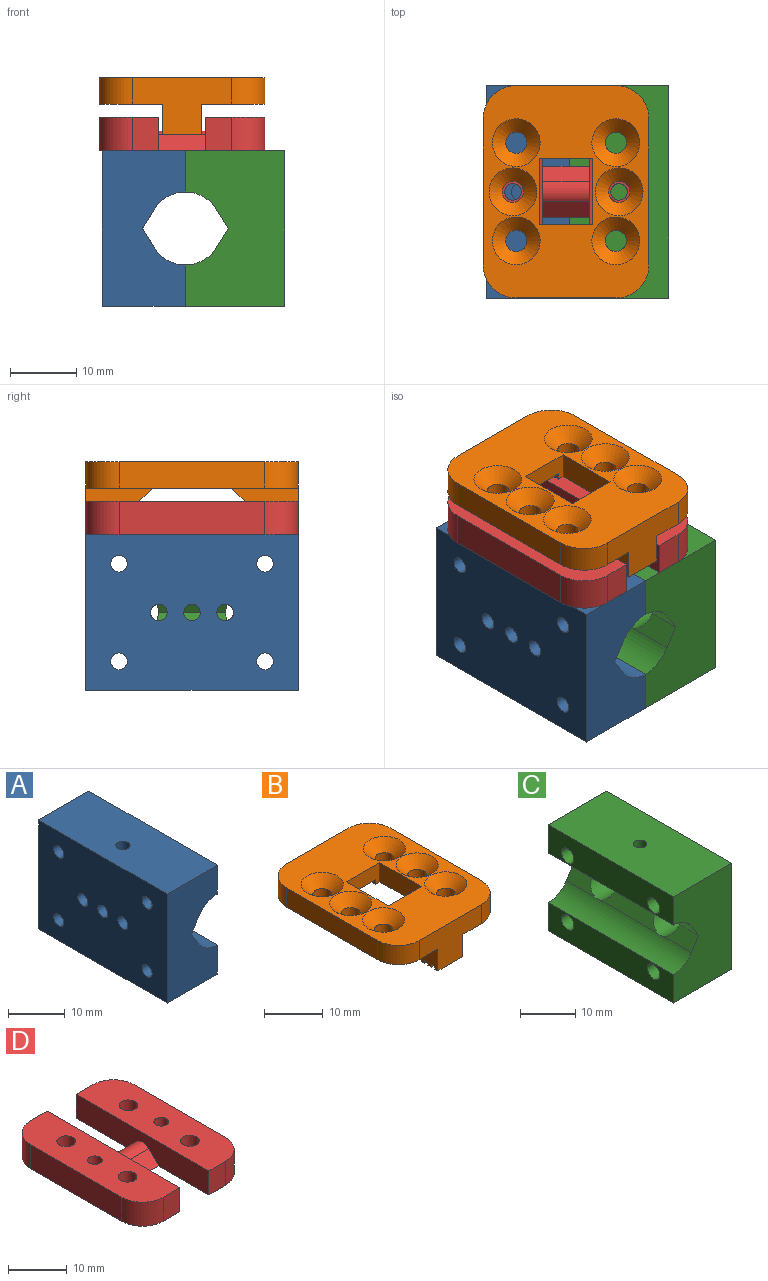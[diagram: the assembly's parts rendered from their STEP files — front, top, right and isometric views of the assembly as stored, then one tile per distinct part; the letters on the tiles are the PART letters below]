
ASSEMBLY  parts=4 mates=3
PART A: 20 faces, bbox 12.5x32x23.5 mm
  f0: plane 2.5x2.5mm, normal (0,0,1), area 4.9mm2, adj f6
  f1: cylinder r=1.25mm len=6.79mm, axis (1,0,0), area 51.1mm2, adj f4,f5,f13
  f2: cylinder r=1.25mm len=6.79mm, axis (1,0,0), area 51.1mm2, adj f4,f5,f13
  f3: cylinder r=1.25mm len=6.79mm, axis (1,0,0), area 51.1mm2, adj f4,f5,f13
  f4: plane 32x2.93mm, normal (0.85,0,0.53), area 102.1mm2, adj f1,f2,f3,f5,f16,f17,f18
  f5: plane 32x2.93mm, normal (0.85,0,-0.53), area 102.1mm2, adj f1,f2,f3,f4,f16,f17,f19
  f6: cylinder r=1.25mm len=10mm, axis (0,0,1), area 78.5mm2, adj f0,f14
  f7: cylinder r=1.25mm len=12.5mm, axis (1,0,0), area 98.2mm2, adj f12,f13
  f8: cylinder r=1.25mm len=12.5mm, axis (1,0,0), area 98.2mm2, adj f10,f13
  f9: cylinder r=1.25mm len=12.5mm, axis (1,0,0), area 98.2mm2, adj f10,f13
  f10: plane 32x6.25mm, normal (1,0,0), area 190.2mm2, adj f8,f9,f14,f16,f17,f19
  f11: cylinder r=1.25mm len=12.5mm, axis (1,0,0), area 98.2mm2, adj f12,f13
  f12: plane 32x6.25mm, normal (1,0,0), area 190.2mm2, adj f7,f11,f15,f16,f17,f18
  f13: plane 32x23.5mm, normal (-1,0,0), area 717.6mm2, adj f1,f2,f3,f7,f8,f9,f11,f14
  f14: plane 32x12.5mm, normal (0,0,1), area 395.1mm2, adj f6,f10,f13,f16,f17
  f15: plane 32x12.5mm, normal (0,0,-1), area 400mm2, adj f12,f13,f16,f17
  f16: plane 23.5x12.5mm, normal (0,1,0), area 244.2mm2, adj f4,f5,f10,f12,f13,f14,f15,f18
  f17: plane 23.5x12.5mm, normal (0,-1,0), area 244.2mm2, adj f4,f5,f10,f12,f13,f14,f15,f18
  f18: cylinder r=5.5mm len=32mm, axis (0,-1,0), area 177.5mm2, adj f4,f12,f16,f17
  f19: cylinder r=5.5mm len=32mm, axis (0,-1,0), area 177.5mm2, adj f5,f10,f16,f17
PART B: 59 faces, bbox 25x32x8.6 mm
  f0: plane 6x0.6mm, normal (0,1,0), area 3.6mm2, adj f1,f14,f15,f16
  f1: plane 6x0.8mm, normal (0,0,-1), area 4.8mm2, adj f0,f2,f15,f16
  f2: plane 6x0.6mm, normal (0,-1,0), area 3.6mm2, adj f1,f3,f15,f16
  f3: plane 6x0.8mm, normal (0,0,-1), area 4.8mm2, adj f2,f4,f15,f16
  f4: plane 6x0.6mm, normal (0,1,0), area 3.6mm2, adj f3,f5,f15,f16
  f5: plane 6x2mm, normal (0,0,-1), area 12mm2, adj f4,f6,f15,f16
  f6: plane 6x5mm, normal (0,0.71,-0.71), area 42.4mm2, adj f5,f7,f15,f16,f18,f24
  f7: plane 8x4mm, normal (0,1,0), area 26mm2, adj f6,f8,f18,f19,f20,f24,f25,f26
  f8: plane 32x25mm, normal (0,0,1), area 454.2mm2, adj f7,f9,f17,f20,f23,f26,f36,f37
  f9: plane 15x8.6mm, normal (0,-1,0), area 87.6mm2, adj f8,f10,f15,f16,f19,f25,f51,f52
  f10: plane 6x0.8mm, normal (0,0,-1), area 4.8mm2, adj f9,f11,f15,f16
  f11: plane 6x0.6mm, normal (0,1,0), area 3.6mm2, adj f10,f12,f15,f16
  f12: plane 6x0.8mm, normal (0,0,-1), area 4.8mm2, adj f11,f13,f15,f16
  f13: plane 6x0.6mm, normal (0,-1,0), area 3.6mm2, adj f12,f14,f15,f16
  f14: plane 6x0.8mm, normal (0,0,-1), area 4.8mm2, adj f0,f13,f15,f16
  f15: plane 10x4.6mm, normal (-1,0,0), area 33.4mm2, adj f0,f1,f2,f3,f4,f5,f6,f9
  f16: plane 10x4.6mm, normal (1,0,0), area 33.4mm2, adj f0,f1,f2,f3,f4,f5,f6,f9
  f17: plane 22x4mm, normal (-1,0,0), area 88mm2, adj f8,f19,f50,f52
  f18: plane 1x1mm, normal (1,0,0), area 0.5mm2, adj f6,f7,f19
  f19: plane 32x9.5mm, normal (0,0,-1), area 259.1mm2, adj f7,f9,f15,f17,f18,f20,f21,f22
  f20: plane 10x4mm, normal (1,0,0), area 40mm2, adj f7,f8,f19,f36
  f21: cylinder r=1.6mm len=3.2mm, axis (0,0,-1), area 20.1mm2, adj f19,f58
  f22: cylinder r=1.6mm len=3.2mm, axis (0,0,-1), area 20.1mm2, adj f19,f56
  f23: plane 22x4mm, normal (1,0,0), area 88mm2, adj f8,f25,f49,f51
  f24: plane 1x1mm, normal (-1,0,0), area 0.5mm2, adj f6,f7,f25
  f25: plane 32x9.5mm, normal (0,0,-1), area 259.1mm2, adj f7,f9,f16,f23,f24,f26,f27,f28
  f26: plane 10x4mm, normal (-1,0,0), area 40mm2, adj f7,f8,f25,f36
  f27: cylinder r=1.6mm len=3.2mm, axis (0,0,-1), area 20.1mm2, adj f25,f57
  f28: cylinder r=1.6mm len=3.2mm, axis (0,0,-1), area 20.1mm2, adj f25,f55
  f29: plane 6x0.6mm, normal (0,-1,0), area 3.6mm2, adj f30,f42,f43,f44
  f30: plane 6x0.8mm, normal (0,0,-1), area 4.8mm2, adj f29,f31,f43,f44
  f31: plane 6x0.6mm, normal (0,1,0), area 3.6mm2, adj f30,f32,f43,f44
  f32: plane 6x0.8mm, normal (0,0,-1), area 4.8mm2, adj f31,f33,f43,f44
  f33: plane 6x0.6mm, normal (0,-1,0), area 3.6mm2, adj f32,f34,f43,f44
  f34: plane 6x2mm, normal (0,0,-1), area 12mm2, adj f33,f35,f43,f44
  f35: plane 6x5mm, normal (0,-0.71,-0.71), area 42.4mm2, adj f34,f36,f43,f44,f45,f47
  f36: plane 8x4mm, normal (0,-1,0), area 26mm2, adj f8,f19,f20,f25,f26,f35,f45,f47
  f37: plane 15x8.6mm, normal (0,1,0), area 87.6mm2, adj f8,f19,f25,f38,f43,f44,f49,f50
  f38: plane 6x0.8mm, normal (0,0,-1), area 4.8mm2, adj f37,f39,f43,f44
  f39: plane 6x0.6mm, normal (0,-1,0), area 3.6mm2, adj f38,f40,f43,f44
  f40: plane 6x0.8mm, normal (0,0,-1), area 4.8mm2, adj f39,f41,f43,f44
  f41: plane 6x0.6mm, normal (0,1,0), area 3.6mm2, adj f40,f42,f43,f44
  f42: plane 6x0.8mm, normal (0,0,-1), area 4.8mm2, adj f29,f41,f43,f44
  f43: plane 10x4.6mm, normal (-1,0,0), area 33.4mm2, adj f19,f29,f30,f31,f32,f33,f34,f35
  f44: plane 10x4.6mm, normal (1,0,0), area 33.4mm2, adj f25,f29,f30,f31,f32,f33,f34,f35
  f45: plane 1x1mm, normal (1,0,0), area 0.5mm2, adj f19,f35,f36
  f46: cylinder r=1.6mm len=3.2mm, axis (0,0,-1), area 20.1mm2, adj f19,f53
  f47: plane 1x1mm, normal (-1,0,0), area 0.5mm2, adj f25,f35,f36
  f48: cylinder r=1.6mm len=3.2mm, axis (0,0,-1), area 20.1mm2, adj f25,f54
  f49: cylinder r=5mm len=5mm, axis (0,0,1), area 31.4mm2, adj f8,f23,f25,f37
  f50: cylinder r=5mm len=5mm, axis (0,0,1), area 31.4mm2, adj f8,f17,f19,f37
  f51: cylinder r=5mm len=5mm, axis (0,0,1), area 31.4mm2, adj f8,f9,f23,f25
  f52: cylinder r=5mm len=5mm, axis (0,0,1), area 31.4mm2, adj f8,f9,f17,f19
  f53: cone r=3.6mm half-angle=45deg, axis (0,0,1), area 46.2mm2, adj f8,f46
  f54: cone r=1.6mm half-angle=45deg, axis (0,0,1), area 46.2mm2, adj f8,f48
  f55: cone r=3.6mm half-angle=45deg, axis (0,0,1), area 46.2mm2, adj f8,f28
  f56: cone r=1.6mm half-angle=45deg, axis (0,0,1), area 46.2mm2, adj f8,f22
  f57: cone r=3.6mm half-angle=45deg, axis (0,0,1), area 46.2mm2, adj f8,f27
  f58: cone r=1.6mm half-angle=45deg, axis (0,0,1), area 46.2mm2, adj f8,f21
PART C: 29 faces, bbox 15x32x23.5 mm
  f0: plane 7.31x2.93mm, normal (-0.85,0,-0.53), area 19.2mm2, adj f2,f6,f12,f14
  f1: plane 14.82x2.93mm, normal (-0.85,0,-0.53), area 39.1mm2, adj f2,f4,f13,f14
  f2: cylinder r=5.5mm len=32mm, axis (0,-1,0), area 177.4mm2, adj f0,f1,f6,f7,f11,f13,f14,f27
  f3: cylinder r=5.5mm len=32mm, axis (0,-1,0), area 177.4mm2, adj f4,f5,f6,f7,f12,f13,f14,f28
  f4: plane 14.82x2.93mm, normal (-0.85,0,0.53), area 39.1mm2, adj f1,f3,f13,f14
  f5: plane 7.31x2.93mm, normal (-0.85,0,0.53), area 19.2mm2, adj f3,f7,f11,f13
  f6: plane 23.5x15mm, normal (0,-1,0), area 302.9mm2, adj f0,f2,f3,f8,f9,f10,f12,f27
  f7: plane 23.5x15mm, normal (0,1,0), area 302.9mm2, adj f2,f3,f5,f8,f9,f10,f11,f27
  f8: plane 32x15mm, normal (0,0,1), area 475.1mm2, adj f6,f7,f10,f25,f27
  f9: plane 32x15mm, normal (0,0,-1), area 470.2mm2, adj f6,f7,f10,f15,f16,f28
  f10: plane 32x23.5mm, normal (1,0,0), area 532.6mm2, adj f6,f7,f8,f9,f13,f14,f21,f22
  f11: plane 7.31x2.93mm, normal (-0.85,0,-0.53), area 19.2mm2, adj f2,f5,f7,f13
  f12: plane 7.31x2.93mm, normal (-0.85,0,0.53), area 19.2mm2, adj f0,f3,f6,f14
  f13: cylinder r=3mm len=10.39mm, axis (-1,0,0), area 177.9mm2, adj f1,f2,f3,f4,f5,f10,f11,f16
  f14: cylinder r=3mm len=10.39mm, axis (-1,0,0), area 177.9mm2, adj f0,f1,f2,f3,f4,f10,f12,f15
  f15: cylinder r=1.25mm len=9.02mm, axis (0,0,1), area 69.8mm2, adj f9,f14
  f16: cylinder r=1.25mm len=9.02mm, axis (0,0,1), area 69.8mm2, adj f9,f13
  f17: cylinder r=1.6mm len=13mm, axis (-1,0,0), area 130.7mm2, adj f24,f28
  f18: cylinder r=1.6mm len=13mm, axis (-1,0,0), area 130.7mm2, adj f23,f28
  f19: cylinder r=1.6mm len=13mm, axis (-1,0,0), area 130.7mm2, adj f22,f27
  f20: cylinder r=1.6mm len=13mm, axis (-1,0,0), area 130.7mm2, adj f21,f27
  f21: cone r=3.6mm half-angle=45deg, axis (1,0,0), area 46.2mm2, adj f10,f20
  f22: cone r=3.6mm half-angle=45deg, axis (1,0,0), area 46.2mm2, adj f10,f19
  f23: cone r=3.6mm half-angle=45deg, axis (1,0,0), area 46.2mm2, adj f10,f18
  f24: cone r=3.6mm half-angle=45deg, axis (1,0,0), area 46.2mm2, adj f10,f17
  f25: cylinder r=1.25mm len=10mm, axis (0,0,1), area 78.5mm2, adj f8,f26
  f26: plane 2.5x2.5mm, normal (0,0,1), area 4.9mm2, adj f25
  f27: plane 32x6.25mm, normal (-1,0,0), area 183.9mm2, adj f2,f6,f7,f8,f19,f20
  f28: plane 32x6.25mm, normal (-1,0,0), area 183.9mm2, adj f3,f6,f7,f9,f17,f18
PART D: 24 faces, bbox 25x32x5 mm
  f0: cylinder r=2.12mm len=7mm, axis (-1,0,0), area 23.3mm2, adj f1,f3,f4,f18
  f1: plane 7x2.38mm, normal (0,-0.71,0.71), area 23.5mm2, adj f0,f2,f4,f18
  f2: plane 32x25mm, normal (0,0,-1), area 566.9mm2, adj f1,f3,f4,f5,f6,f7,f8,f9
  f3: plane 7x2.38mm, normal (0,0.71,0.71), area 23.5mm2, adj f0,f2,f4,f18
  f4: plane 32x5mm, normal (1,0,0), area 145.9mm2, adj f0,f1,f2,f3,f5,f9,f11
  f5: plane 5x4mm, normal (0,1,0), area 20mm2, adj f2,f4,f11,f20
  f6: plane 22x5mm, normal (-1,0,0), area 110mm2, adj f2,f11,f20,f21
  f7: cylinder r=1.6mm len=5mm, axis (0,0,-1), area 50.3mm2, adj f2,f11
  f8: cylinder r=1.6mm len=5mm, axis (0,0,-1), area 50.3mm2, adj f2,f11
  f9: plane 5x4mm, normal (0,-1,0), area 20mm2, adj f2,f4,f11,f21
  f10: cylinder r=1.25mm len=5mm, axis (0,0,-1), area 39.3mm2, adj f2,f11
  f11: plane 32x9mm, normal (0,0,1), area 256.3mm2, adj f4,f5,f6,f7,f8,f9,f10,f20
  f12: plane 5x4mm, normal (0,-1,0), area 20mm2, adj f2,f18,f19,f22
  f13: plane 22x5mm, normal (1,0,0), area 110mm2, adj f2,f19,f22,f23
  f14: plane 5x4mm, normal (0,1,0), area 20mm2, adj f2,f18,f19,f23
  f15: cylinder r=1.6mm len=5mm, axis (0,0,-1), area 50.3mm2, adj f2,f19
  f16: cylinder r=1.6mm len=5mm, axis (0,0,-1), area 50.3mm2, adj f2,f19
  f17: cylinder r=1.25mm len=5mm, axis (0,0,-1), area 39.3mm2, adj f2,f19
  f18: plane 32x5mm, normal (-1,0,0), area 145.9mm2, adj f0,f1,f2,f3,f12,f14,f19
  f19: plane 32x9mm, normal (0,0,1), area 256.3mm2, adj f12,f13,f14,f15,f16,f17,f18,f22
  f20: cylinder r=5mm len=5mm, axis (0,0,-1), area 39.3mm2, adj f2,f5,f6,f11
  f21: cylinder r=5mm len=5mm, axis (0,0,1), area 39.3mm2, adj f2,f6,f9,f11
  f22: cylinder r=5mm len=5mm, axis (0,0,1), area 39.3mm2, adj f2,f12,f13,f19
  f23: cylinder r=5mm len=5mm, axis (0,0,-1), area 39.3mm2, adj f2,f13,f14,f19
PLACE A t=(0.5,0,0)mm
PLACE B t=(0,0,2)mm
PLACE C t=(0.5,0,0)mm
PLACE D at identity fixed
MATE fastened C.f25 <-> D.f17  axis (0,0,1) through (8,0,11.75)mm
MATE fastened B.f48 <-> D.f16  axis (0,0,-1) through (7.5,7.4,18.75)mm
MATE fastened A.f9 <-> C.f20  axis (1,0,0) through (0.5,-11,7.35)mm
